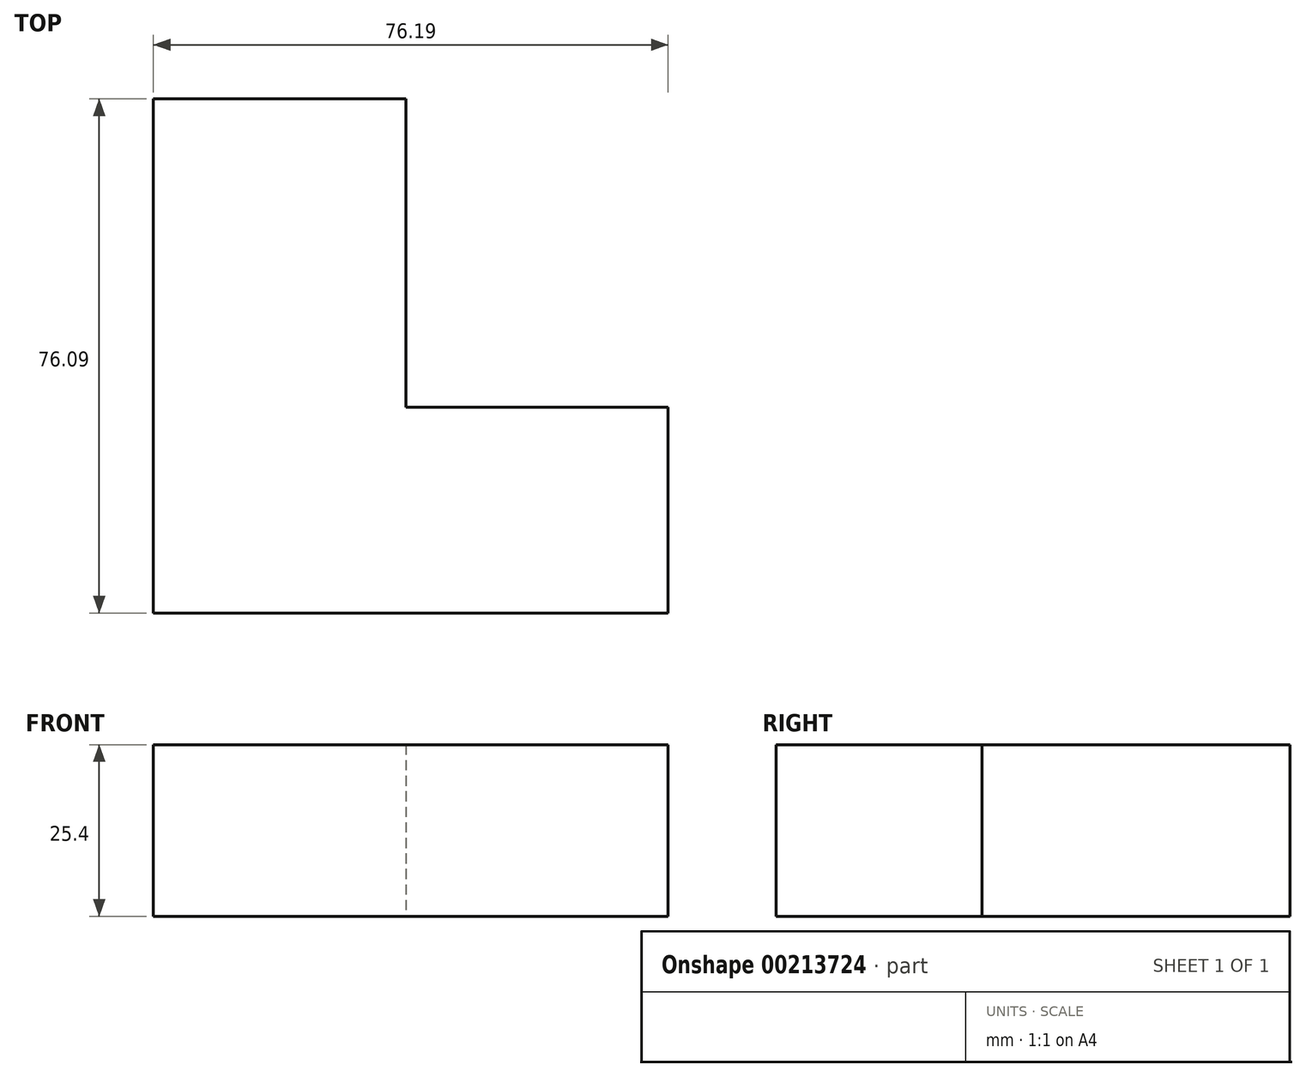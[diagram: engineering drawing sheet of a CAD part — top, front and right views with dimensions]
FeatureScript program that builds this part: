
annotation { "Feature Type Name" : "Feature", "Feature Type Description" : "" }
export const myFeature = defineFeature(function(context is Context, id is Id, definition is map)
    precondition{}
    {
        {
            var Q0;
            Q0=qCreatedBy(makeId("Top.planeOp"),FACE);
            var sketch = newSketch(context, id + "F0", { "sketchPlane" : qUnion([Q0])});
            skLineSegment(sketch, "E0.bottom", {"start": v(0, 0) * mm, "end": v(37.4, 0) * mm});
            skLineSegment(sketch, "E0.top", {"start": v(0, 76.1) * mm, "end": v(37.4, 76.1) * mm});
            skLineSegment(sketch, "E0.left", {"start": v(0, 0) * mm, "end": v(0, 76.1) * mm});
            skLineSegment(sketch, "E0.right", {"start": v(37.4, 0) * mm, "end": v(37.4, 76.1) * mm});
            skLineSegment(sketch, "E1.bottom", {"start": v(37.4, 0) * mm, "end": v(76.2, 0) * mm});
            skLineSegment(sketch, "E1.top", {"start": v(37.4, 30.46) * mm, "end": v(76.2, 30.46) * mm});
            skLineSegment(sketch, "E1.left", {"start": v(37.4, 0) * mm, "end": v(37.4, 30.46) * mm});
            skLineSegment(sketch, "E1.right", {"start": v(76.2, 0) * mm, "end": v(76.2, 30.46) * mm});
            skSolve(sketch);
        }
        {
            var Q0;
            Q0=makeQuery(id+"F0.imprint","IMPRINT",FACE,{"disambiguationData":[TD([[makeQuery(id+"F0.imprint","IMPRINT",EDGE,{"derivedFrom":sQuery(id+"F0.wireOp",EDGE,"E0.bottom")}),1.0]])]});
            var Q1;
            Q1=makeQuery(id+"F0.imprint","IMPRINT",FACE,{"disambiguationData":[TD([[makeQuery(id+"F0.imprint","IMPRINT",EDGE,{"derivedFrom":sQuery(id+"F0.wireOp",EDGE,"E1.bottom")}),1.0]])]});
            extrude(context, id + "F1", {"entities" : qUnion([Q0, Q1]), "depth" : 25.4 * mm});
        }
    });
